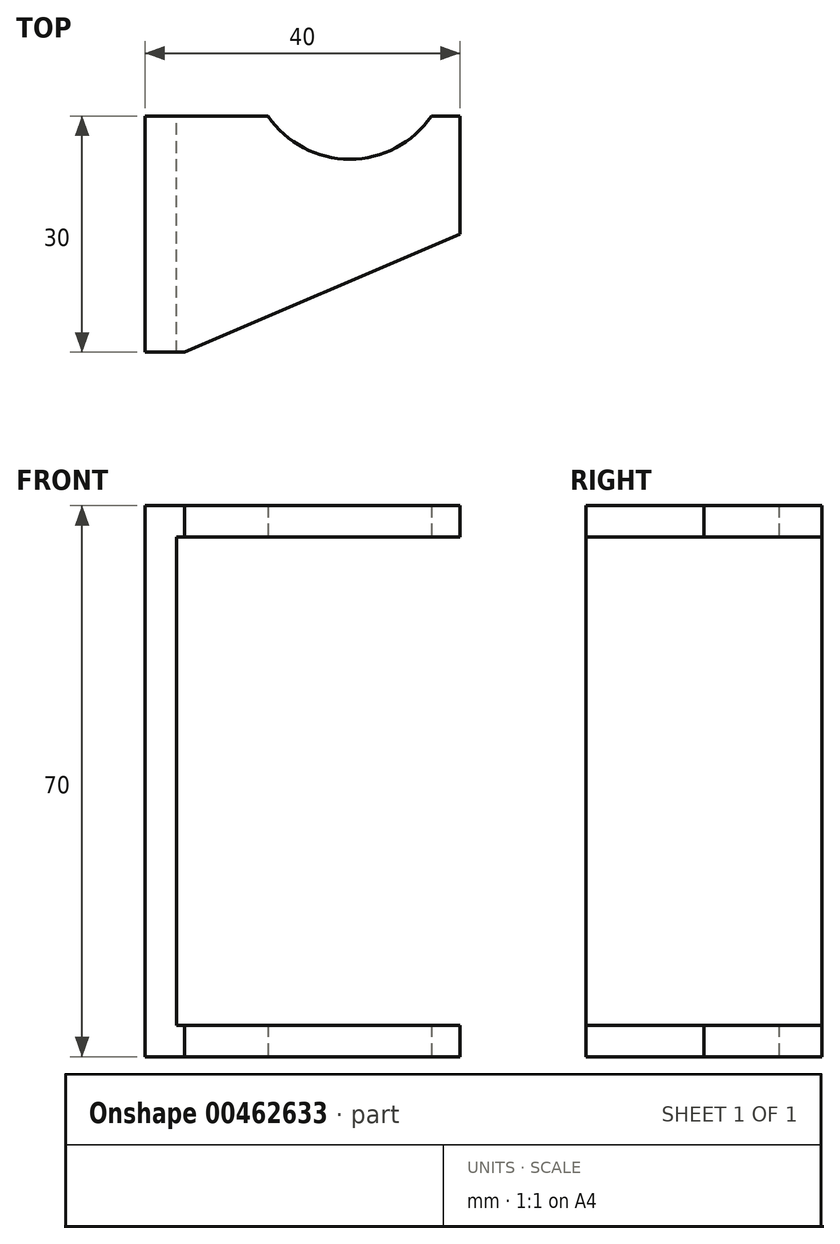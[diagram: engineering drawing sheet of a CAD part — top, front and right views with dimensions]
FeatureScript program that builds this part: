
annotation { "Feature Type Name" : "Feature", "Feature Type Description" : "" }
export const myFeature = defineFeature(function(context is Context, id is Id, definition is map)
    precondition{}
    {
        {
            var Q0;
            Q0=qCreatedBy(makeId("Top.planeOp"),FACE);
            var sketch = newSketch(context, id + "F0", { "sketchPlane" : qUnion([Q0])});
            skLineSegment(sketch, "E0.bottom", {"start": v(20, 15) * mm, "end": v(-20, 15) * mm});
            skLineSegment(sketch, "E0.right", {"start": v(-20, 15) * mm, "end": v(-20, -15) * mm});
            skPoint(sketch, "E0.middle", {"position": v(0, 0) * mm});
            skLineSegment(sketch, "E1", {"start": v(-20, -15) * mm, "end": v(-15, -15) * mm});
            skLineSegment(sketch, "E2", {"start": v(20, 0) * mm, "end": v(-15, -15) * mm});
            skLineSegment(sketch, "E3", {"start": v(20, 15) * mm, "end": v(20, 0) * mm});
            skLineSegment(sketch, "E4", {"start": v(6, 15) * mm, "end": v(6, 22) * mm});
            skCircle(sketch, "E5", {"center": v(6, 22) * mm, "radius": 12.5 * mm});
            skLineSegment(sketch, "E6", {"start": v(6, 15) * mm, "end": v(20, 15) * mm, "construction": true});
            skSolve(sketch);
        }
        {
            var Q0;
            {var subQ0=sQuery(id+"F0.wireOp",EDGE,"E0.right");Q0=makeQuery(id+"F0.imprint","IMPRINT",FACE,{"disambiguationData":[TD([[makeQuery(id+"F0.imprint","IMPRINT",EDGE,{"derivedFrom":subQ0}),1.0]])]});}
            extrude(context, id + "F1", {"entities" : qUnion([Q0]), "endBound" : BoundingType.SYMMETRIC, "depth" : 70 * mm});
        }
        {
            var Q0;
            {var subQ0=sQuery(id+"F0.wireOp",EDGE,"E0.bottom");Q0=makeQuery(id+"F1.opExtrude","SWEPT_FACE",FACE,{"disambiguationData":[OSD([subQ0]),TDD([makeQuery(id+"F0.imprint","IMPRINT",EDGE,{"disambiguationData":[TD([[makeQuery(id+"F0.imprint","INTERSECT",VERTEX,{"derivedFrom":[subQ0,sQuery(id+"F0.wireOp",EDGE,"E0.right")]}),1.0]])],"derivedFrom":subQ0})])]});}
            var sketch = newSketch(context, id + "F2", { "sketchPlane" : qUnion([Q0])});
            skLineSegment(sketch, "E7", {"start": v(16, 35) * mm, "end": v(16, 31) * mm, "construction": true});
            skLineSegment(sketch, "E8", {"start": v(16, 31) * mm, "end": v(20, 31) * mm, "construction": true});
            skLineSegment(sketch, "E9.bottom", {"start": v(16, 31) * mm, "end": v(-38.81, 31) * mm});
            skLineSegment(sketch, "E9.top", {"start": v(16, -31) * mm, "end": v(-38.81, -31) * mm});
            skLineSegment(sketch, "E9.left", {"start": v(16, 31) * mm, "end": v(16, -31) * mm});
            skLineSegment(sketch, "E9.right", {"start": v(-38.81, 31) * mm, "end": v(-38.81, -31) * mm});
            skLineSegment(sketch, "E10", {"start": v(16, -31) * mm, "end": v(20, -31) * mm});
            skLineSegment(sketch, "E11", {"start": v(16, -31) * mm, "end": v(16, -35) * mm});
            skSolve(sketch);
        }
        {
            var Q0;
            {var subQ0=sQuery(id+"F2.wireOp",EDGE,"E9.right");Q0=makeQuery(id+"F2.imprint","IMPRINT",FACE,{"disambiguationData":[TD([[makeQuery(id+"F2.imprint","IMPRINT",EDGE,{"derivedFrom":subQ0}),1.0]])]});}
            var Q1;
            {var subQ0=sQuery(id+"F2.wireOp",EDGE,"E9.left");Q1=makeQuery(id+"F2.imprint","IMPRINT",FACE,{"disambiguationData":[TD([[makeQuery(id+"F2.imprint","IMPRINT",EDGE,{"derivedFrom":subQ0}),-1.0]])]});}
            extrude(context, id + "F3", {"entities" : qUnion([Q0, Q1]), "operationType" : NewBodyOperationType.REMOVE, "oppositeDirection" : true, "depth" : 40 * mm});
        }
    });
